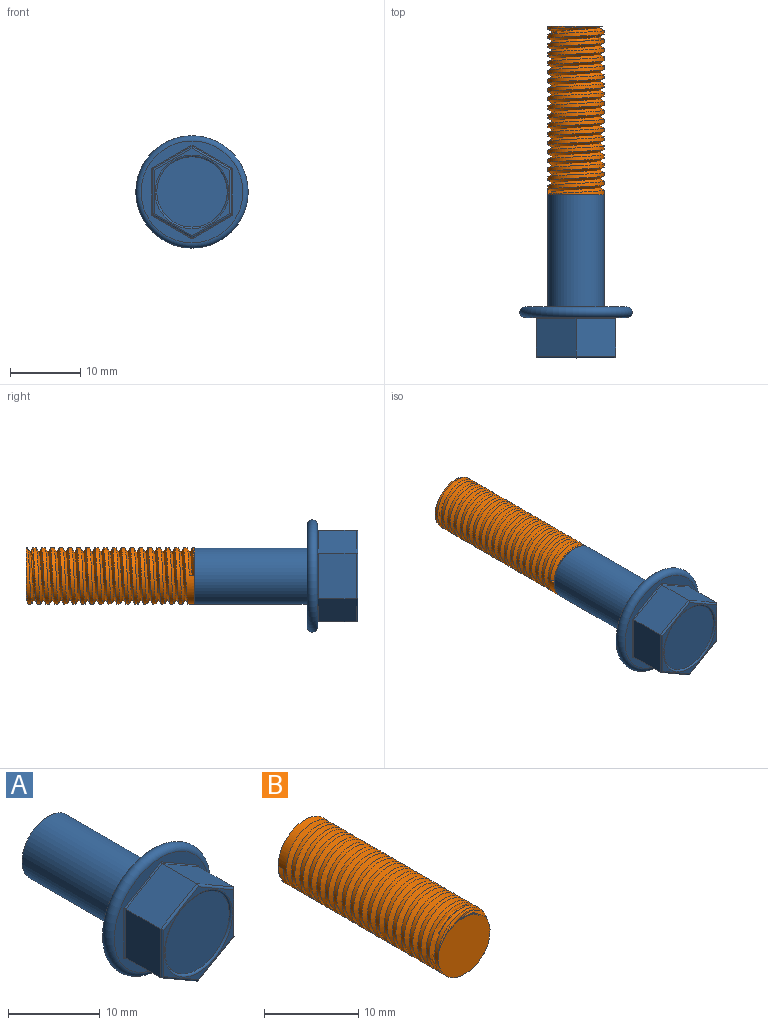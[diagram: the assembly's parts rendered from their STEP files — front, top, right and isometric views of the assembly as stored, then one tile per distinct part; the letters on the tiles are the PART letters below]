
ASSEMBLY  parts=2 mates=1
PART A: 26 faces, bbox 17.3x23.3x17.3 mm
  f0: plane 14.5x14.5mm, normal (0,-1,0), area 49.4mm2, adj f10,f11,f12,f13,f14,f15,f16
  f1: cylinder r=4mm len=16mm, axis (0,1,0), area 402.1mm2, adj f2,f3
  f2: plane 8x8mm, normal (0,1,0), area 50.3mm2, adj f1
  f3: plane 14.5x14.5mm, normal (0,1,0), area 114.9mm2, adj f1,f10
  f4: plane 5.63x5.35mm, normal (-0.5,0,0.87), area 34.8mm2, adj f5,f9,f12,f21
  f5: plane 6.5x5.35mm, normal (-1,0,0), area 34.8mm2, adj f4,f6,f11,f20
  f6: plane 5.63x5.35mm, normal (-0.5,0,-0.87), area 34.8mm2, adj f5,f7,f13,f22
  f7: plane 5.63x5.35mm, normal (0.5,0,-0.87), area 34.8mm2, adj f6,f8,f15,f24
  f8: plane 6.5x5.35mm, normal (1,0,0), area 34.8mm2, adj f7,f9,f16,f25
  f9: plane 5.63x5.35mm, normal (0.5,0,0.87), area 34.8mm2, adj f4,f8,f14,f23
  f10: torus R=7.25mm, axis (0,-1,0), area 114.4mm2, adj f0,f3
  f11: cylinder r=0.15mm len=6.67mm, axis (0,0,-1), area 1.5mm2, adj f0,f5,f12,f13
  f12: cylinder r=0.15mm len=5.85mm, axis (-0.87,0,-0.5), area 1.5mm2, adj f0,f4,f11,f14
  f13: cylinder r=0.15mm len=5.85mm, axis (0.87,0,-0.5), area 1.5mm2, adj f0,f6,f11,f15
  f14: cylinder r=0.15mm len=5.85mm, axis (-0.87,0,0.5), area 1.5mm2, adj f0,f9,f12,f16
  f15: cylinder r=0.15mm len=5.85mm, axis (0.87,0,0.5), area 1.5mm2, adj f0,f7,f13,f16
  f16: cylinder r=0.15mm len=6.67mm, axis (0,0,1), area 1.5mm2, adj f0,f8,f14,f15
  f17: plane 12.42x10.76mm, normal (0,-1,0), area 13.6mm2, adj f19,f20,f21,f22,f23,f24,f25
  f18: plane 10x10mm, normal (0,-1,0), area 78.5mm2, adj f19
  f19: torus R=5.25mm, axis (0,-1,0), area 12.6mm2, adj f17,f18
  f20: cylinder r=0.25mm len=6.5mm, axis (0,0,1), area 2.5mm2, adj f5,f17,f21,f22
  f21: cylinder r=0.25mm len=5.75mm, axis (0.87,0,0.5), area 2.5mm2, adj f4,f17,f20,f23
  f22: cylinder r=0.25mm len=5.75mm, axis (-0.87,0,0.5), area 2.5mm2, adj f6,f17,f20,f24
  f23: cylinder r=0.25mm len=5.75mm, axis (0.87,0,-0.5), area 2.5mm2, adj f9,f17,f21,f25
  f24: cylinder r=0.25mm len=5.75mm, axis (-0.87,0,-0.5), area 2.5mm2, adj f7,f17,f22,f25
  f25: cylinder r=0.25mm len=6.5mm, axis (0,0,-1), area 2.5mm2, adj f8,f17,f23,f24
PART B: 6 faces, bbox 8.3x24.7x8.3 mm
  f0: cylinder r=4mm len=24mm, axis (0,1,0), area 253.3mm2, adj f1,f2,f3,f4,f5
  f1: plane 8.12x7.8mm, normal (0,-1,0), area 45.5mm2, adj f0,f4,f5
  f2: plane 8x8mm, normal (0,1,0), area 50.3mm2, adj f0
  f3: plane 0.76x0.67mm, normal (0,0,-1), area 0.2mm2, adj f0,f4,f5
  f4: bspline ~24.37x8mm, area 330.5mm2, adj f0,f1,f3,f5
  f5: bspline ~23.99x7.99mm, area 322.5mm2, adj f0,f1,f3,f4
PLACE A t=(-7.58,1.52,-8.62)mm
PLACE B rot(axis=(1,0,0),180deg) t=(-7.58,1.52,-8.62)mm
MATE planar B.f0 <-> A.f1  axis (0,-1,0) through (-7.58,1.52,-8.62)mm
